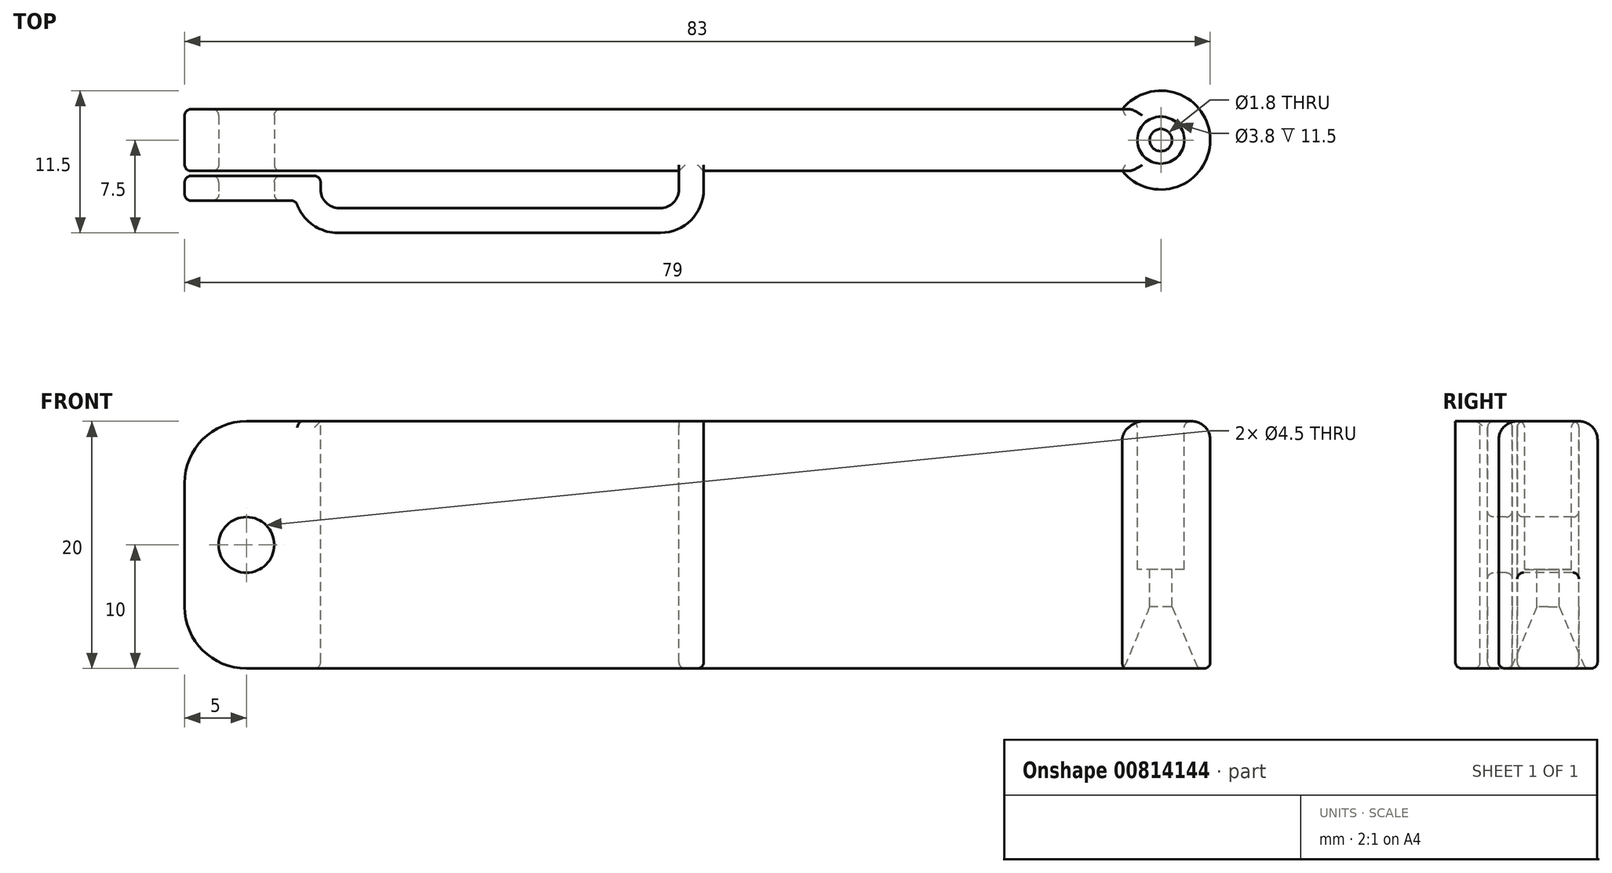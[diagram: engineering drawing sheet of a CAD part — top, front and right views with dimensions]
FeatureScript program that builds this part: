
annotation { "Feature Type Name" : "Feature", "Feature Type Description" : "" }
export const myFeature = defineFeature(function(context is Context, id is Id, definition is map)
    precondition{}
    {
        {
            var Q0;
            Q0=qCreatedBy(makeId("Front.planeOp"),FACE);
            var sketch = newSketch(context, id + "F0", { "sketchPlane" : qUnion([Q0])});
            skLineSegment(sketch, "E0.bottom", {"start": v(5, -20) * mm, "end": v(75, -20) * mm});
            skLineSegment(sketch, "E0.top", {"start": v(5, 0) * mm, "end": v(75, 0) * mm});
            skLineSegment(sketch, "E0.left", {"start": v(0, -15) * mm, "end": v(0, -5) * mm});
            skLineSegment(sketch, "E0.right", {"start": v(75, -20) * mm, "end": v(75, 0) * mm});
            skCircle(sketch, "E1", {"center": v(5, -10) * mm, "radius": 2.25 * mm});
            skPoint(sketch, "E2", {"position": v(0, -10) * mm});
            skPoint(sketch, "E3.visualSharp", {"position": v(0, 0) * mm});
            skArc(sketch, "E3.filletArc", {"start": v(5, 0) * mm, "mid": v(1.46, -1.46) * mm, "end": v(0, -5) * mm});
            skPoint(sketch, "E4.visualSharp", {"position": v(0, -20) * mm});
            skArc(sketch, "E4.filletArc", {"start": v(0, -15) * mm, "mid": v(1.46, -18.54) * mm, "end": v(5, -20) * mm});
            skSolve(sketch);
        }
        {
            var Q0;
            Q0 = qSketchRegion(id + "F0", true);
            extrude(context, id + "F1", {"entities" : qUnion([Q0]), "oppositeDirection" : true, "depth" : 5 * mm, "offsetDistance" : 25 * mm});
        }
        {
            var Q0;
            Q0=makeQuery(id+"F1.opExtrude","SWEPT_FACE",FACE,{"disambiguationData":[OSD([sQuery(id+"F0.wireOp",EDGE,"E0.top")])]});
            var sketch = newSketch(context, id + "F2", { "sketchPlane" : qUnion([Q0])});
            skLineSegment(sketch, "E5", {"start": v(0, 0) * mm, "end": v(11, 0) * mm});
            skLineSegment(sketch, "E6", {"start": v(11, 0) * mm, "end": v(11, -3) * mm});
            skLineSegment(sketch, "E7", {"start": v(11, -3) * mm, "end": v(40, -3) * mm});
            skLineSegment(sketch, "E8", {"start": v(40, -3) * mm, "end": v(40, 0) * mm});
            skLineSegment(sketch, "E9", {"start": v(40, 0) * mm, "end": v(42, 0) * mm});
            skLineSegment(sketch, "E10", {"start": v(42, 0) * mm, "end": v(42, -5) * mm});
            skLineSegment(sketch, "E11", {"start": v(42, -5) * mm, "end": v(9, -5) * mm});
            skLineSegment(sketch, "E12", {"start": v(9, -5) * mm, "end": v(9, -2.4) * mm});
            skLineSegment(sketch, "E13", {"start": v(0, -2.4) * mm, "end": v(0, 0) * mm});
            skLineSegment(sketch, "E14", {"start": v(0, -2.4) * mm, "end": v(9, -2.4) * mm});
            skSolve(sketch);
        }
        {
            var Q0;
            Q0 = qSketchRegion(id + "F2", true);
            var Q1;
            Q1=makeQuery(id+"F1.opExtrude","SWEPT_FACE",FACE,{"disambiguationData":[OSD([sQuery(id+"F0.wireOp",EDGE,"E0.bottom")])]});
            extrude(context, id + "F3", {"entities" : qUnion([Q0]), "operationType" : NewBodyOperationType.ADD, "endBound" : BoundingType.UP_TO_SURFACE, "oppositeDirection" : true, "depth" : 25 * mm, "endBoundEntityFace" : qUnion([Q1]), "offsetDistance" : 25 * mm});
        }
        {
            var Q0;
            Q0=makeQuery(id+"F1.opExtrude","CAP_FACE",FACE,{"disambiguationData":[OSD([sQuery(id+"F0.wireOp",EDGE,"E0.bottom"),sQuery(id+"F0.wireOp",EDGE,"E0.top"),sQuery(id+"F0.wireOp",EDGE,"E0.left"),sQuery(id+"F0.wireOp",EDGE,"E0.right"),sQuery(id+"F0.wireOp",EDGE,"E1"),sQuery(id+"F0.wireOp",EDGE,"E3.filletArc"),sQuery(id+"F0.wireOp",EDGE,"E4.filletArc")])],"isStart":false});
            var sketch = newSketch(context, id + "F4", { "sketchPlane" : qUnion([Q0])});
            skCircle(sketch, "E15", {"center": v(-5, -10) * mm, "radius": 2.25 * mm});
            skSolve(sketch);
        }
        {
            var Q0;
            Q0 = qSketchRegion(id + "F4", true);
            extrude(context, id + "F5", {"entities" : qUnion([Q0]), "operationType" : NewBodyOperationType.REMOVE, "endBound" : BoundingType.THROUGH_ALL, "oppositeDirection" : true, "depth" : 25 * mm, "offsetDistance" : 25 * mm});
        }
        {
            var Q0;
            Q0=makeQuery(id+"F3.opExtrude","CAP_EDGE",EDGE,{"disambiguationData":[OSD([sQuery(id+"F2.wireOp",EDGE,"E13")])],"isStart":false});
            var Q1;
            Q1=makeQuery(id+"F3.opExtrude","CAP_EDGE",EDGE,{"disambiguationData":[OSD([sQuery(id+"F2.wireOp",EDGE,"E13")])],"isStart":true});
            fillet(context, id + "F6", {"entities" : qUnion([Q0, Q1]), "radius" : 5 * mm, "tangentPropagation" : true, "allowEdgeOverflow" : false});
        }
        {
            var Q0;
            Q0=makeQuery(id+"F3.boolean.opBoolean","MERGE",FACE,{"derivedFrom":[makeQuery(id+"F1.opExtrude","SWEPT_FACE",FACE,{"disambiguationData":[OSD([sQuery(id+"F0.wireOp",EDGE,"E0.bottom")])]}),makeQuery(id+"F3.opExtrude","CAP_FACE",FACE,{"disambiguationData":[OSD([sQuery(id+"F2.wireOp",EDGE,"E5"),sQuery(id+"F2.wireOp",EDGE,"E6"),sQuery(id+"F2.wireOp",EDGE,"E7"),sQuery(id+"F2.wireOp",EDGE,"E8"),sQuery(id+"F2.wireOp",EDGE,"E9"),sQuery(id+"F2.wireOp",EDGE,"E10"),sQuery(id+"F2.wireOp",EDGE,"E11"),sQuery(id+"F2.wireOp",EDGE,"E12"),sQuery(id+"F2.wireOp",EDGE,"oNY84z7X-RgDA-BSrN-n4GT-R6lyssik0dSa"),sQuery(id+"F2.wireOp",EDGE,"E13")])],"isStart":false})]});
            var sketch = newSketch(context, id + "F7", { "sketchPlane" : qUnion([Q0])});
            skLineSegment(sketch, "E16.bottom", {"start": v(12.2, 0) * mm, "end": v(-0.8, 0) * mm});
            skLineSegment(sketch, "E16.top", {"start": v(12.2, 0.4) * mm, "end": v(-0.8, 0.4) * mm});
            skLineSegment(sketch, "E16.left", {"start": v(12.2, 0) * mm, "end": v(12.2, 0.4) * mm});
            skLineSegment(sketch, "E16.right", {"start": v(-0.8, 0) * mm, "end": v(-0.8, 0.4) * mm});
            skSolve(sketch);
        }
        {
            var Q0;
            Q0 = qSketchRegion(id + "F7", true);
            extrude(context, id + "F8", {"entities" : qUnion([Q0]), "operationType" : NewBodyOperationType.REMOVE, "endBound" : BoundingType.THROUGH_ALL, "oppositeDirection" : true, "depth" : 25 * mm, "offsetDistance" : 25 * mm});
        }
        {
            var Q0;
            Q0=makeQuery(id+"F1.opExtrude","SWEPT_EDGE",EDGE,{"disambiguationData":[OSD([sQuery(id+"F0.wireOp",EDGE,"E0.top"),sQuery(id+"F0.wireOp",EDGE,"E0.right")])]});
            cPoint(context, id + "F9", {"entities" : qUnion([Q0]), "parameter" : 0.5});
        }
        {
            var Q0;
            Q0=makeQuery(id+"F1.opExtrude","CAP_FACE",FACE,{"disambiguationData":[OSD([sQuery(id+"F0.wireOp",EDGE,"E0.bottom"),sQuery(id+"F0.wireOp",EDGE,"E0.top"),sQuery(id+"F0.wireOp",EDGE,"E0.left"),sQuery(id+"F0.wireOp",EDGE,"E0.right"),sQuery(id+"F0.wireOp",EDGE,"E1"),sQuery(id+"F0.wireOp",EDGE,"E3.filletArc"),sQuery(id+"F0.wireOp",EDGE,"E4.filletArc")])],"isStart":false});
            var Q1;
            Q1 = qCreatedBy(id + "F9" ,VERTEX);
            cPlane(context, id + "F10", {"entities" : qUnion([Q0, Q1]), "cplaneType" : CPlaneType.PLANE_POINT, "offset" : 25 * mm, "oppositeDirection" : true, "width" : 150 * mm, "height" : 150 * mm});
        }
        {
            var Q0;
            Q0=qCreatedBy(id+"F10.planeOp",FACE);
            var sketch = newSketch(context, id + "F11", { "sketchPlane" : qUnion([Q0])});
            skLineSegment(sketch, "E17", {"start": v(-78.1, -12) * mm, "end": v(-78.1, -15) * mm});
            skLineSegment(sketch, "E18", {"start": v(-78.1, -15) * mm, "end": v(-76, -20) * mm});
            skLineSegment(sketch, "E19", {"start": v(-76, -20) * mm, "end": v(-75, -20) * mm});
            skLineSegment(sketch, "E20", {"start": v(-75, -20) * mm, "end": v(-75, 0) * mm});
            skLineSegment(sketch, "E21", {"start": v(-75, 0) * mm, "end": v(-77.1, 0) * mm});
            skLineSegment(sketch, "E22", {"start": v(-79, 5.76) * mm, "end": v(-79, -23.82) * mm, "construction": true});
            skLineSegment(sketch, "E23", {"start": v(-77.1, 0) * mm, "end": v(-77.1, -12) * mm});
            skLineSegment(sketch, "E24", {"start": v(-77.1, -12) * mm, "end": v(-78.1, -12) * mm});
            skSolve(sketch);
        }
        {
            var Q0;
            Q0 = qSketchRegion(id + "F11", true);
            var Q1;
            Q1=sQuery(id+"F11.wireOp",EDGE,"E22");
            revolve(context, id + "F12", {"operationType" : NewBodyOperationType.ADD, "surfaceOperationType" : NewSurfaceOperationType.NEW, "entities" : qUnion([Q0]), "axis" : qUnion([Q1]), "revolveType" : RevolveType.FULL});
        }
        {
            var Q0;
            Q0=makeQuery(id+"F1.opExtrude","SWEPT_FACE",FACE,{"disambiguationData":[OSD([sQuery(id+"F0.wireOp",EDGE,"E0.right")])]});
            var sketch = newSketch(context, id + "F13", { "sketchPlane" : qUnion([Q0])});
            skLineSegment(sketch, "E25.bottom", {"start": v(5, 0) * mm, "end": v(0, 0) * mm});
            skLineSegment(sketch, "E25.top", {"start": v(5, -20) * mm, "end": v(0, -20) * mm});
            skLineSegment(sketch, "E25.left", {"start": v(5, 0) * mm, "end": v(5, -20) * mm});
            skLineSegment(sketch, "E25.right", {"start": v(0, 0) * mm, "end": v(0, -20) * mm});
            skSolve(sketch);
        }
        {
            var Q0;
            Q0 = qSketchRegion(id + "F13", true);
            var Q1;
            Q1=makeQuery(id+"F12.opRevolve","SWEPT_BODY",BODY,{"disambiguationData":[OSD([sQuery(id+"F11.wireOp",EDGE,"E17"),sQuery(id+"F11.wireOp",EDGE,"E18"),sQuery(id+"F11.wireOp",EDGE,"E19"),sQuery(id+"F11.wireOp",EDGE,"E20"),sQuery(id+"F11.wireOp",EDGE,"E21")])]});
            extrude(context, id + "F14", {"entities" : qUnion([Q0]), "operationType" : NewBodyOperationType.ADD, "depth" : 1 * mm, "endBoundEntityBody" : qUnion([Q1]), "offsetDistance" : 25 * mm});
        }
        {
            var Q0;
            Q0=makeQuery(id+"F3.opExtrude","SWEPT_EDGE",EDGE,{"disambiguationData":[OSD([sQuery(id+"F2.wireOp",EDGE,"E10"),sQuery(id+"F2.wireOp",EDGE,"E11")])]});
            var Q1;
            Q1=makeQuery(id+"F3.opExtrude","SWEPT_EDGE",EDGE,{"disambiguationData":[OSD([sQuery(id+"F2.wireOp",EDGE,"E11"),sQuery(id+"F2.wireOp",EDGE,"E12")])]});
            fillet(context, id + "F15", {"entities" : qUnion([Q0, Q1]), "radius" : 3.5 * mm, "tangentPropagation" : true, "allowEdgeOverflow" : false});
        }
        {
            var Q0;
            Q0=makeQuery(id+"F3.opExtrude","SWEPT_EDGE",EDGE,{"disambiguationData":[OSD([sQuery(id+"F2.wireOp",EDGE,"E7"),sQuery(id+"F2.wireOp",EDGE,"E8")])]});
            var Q1;
            Q1=makeQuery(id+"F3.opExtrude","SWEPT_EDGE",EDGE,{"disambiguationData":[OSD([sQuery(id+"F0.wireOp",EDGE,"E0.top"),sQuery(id+"F2.wireOp",EDGE,"E8"),sQuery(id+"F2.wireOp",EDGE,"E9")])]});
            var Q2;
            Q2=makeQuery(id+"F3.opExtrude","SWEPT_EDGE",EDGE,{"disambiguationData":[OSD([sQuery(id+"F2.wireOp",EDGE,"E6"),sQuery(id+"F2.wireOp",EDGE,"E7")])]});
            var Q3;
            Q3=makeQuery(id+"F3.opExtrude","SWEPT_EDGE",EDGE,{"disambiguationData":[OSD([sQuery(id+"F0.wireOp",EDGE,"E0.top"),sQuery(id+"F2.wireOp",EDGE,"E9"),sQuery(id+"F2.wireOp",EDGE,"E10")])]});
            fillet(context, id + "F16", {"entities" : qUnion([Q0, Q1, Q2, Q3]), "radius" : 1.5 * mm, "tangentPropagation" : true, "allowEdgeOverflow" : false});
        }
        {
            var Q0;
            Q0=makeQuery(id+"F12.opRevolve","SWEPT_EDGE",EDGE,{"disambiguationData":[OSD([sQuery(id+"F11.wireOp",EDGE,"E20"),sQuery(id+"F11.wireOp",EDGE,"E21")])]});
            fillet(context, id + "F17", {"entities" : qUnion([Q0]), "radius" : 1.5 * mm, "tangentPropagation" : true, "defaultsChanged" : true, "vertexSettings" : [], "allowEdgeOverflow" : false});
        }
        {
            var Q0;
            Q0=makeQuery(id+"F14.boolean.opBoolean","MERGE",FACE,{"derivedFrom":[makeQuery(id+"F3.boolean.opBoolean","MERGE",FACE,{"derivedFrom":[makeQuery(id+"F1.opExtrude","SWEPT_FACE",FACE,{"disambiguationData":[OSD([sQuery(id+"F0.wireOp",EDGE,"E0.bottom")])]}),makeQuery(id+"F3.opExtrude","CAP_FACE",FACE,{"disambiguationData":[OSD([sQuery(id+"F2.wireOp",EDGE,"E5"),sQuery(id+"F2.wireOp",EDGE,"E6"),sQuery(id+"F2.wireOp",EDGE,"E7"),sQuery(id+"F2.wireOp",EDGE,"E8"),sQuery(id+"F2.wireOp",EDGE,"E9"),sQuery(id+"F2.wireOp",EDGE,"E10"),sQuery(id+"F2.wireOp",EDGE,"E11"),sQuery(id+"F2.wireOp",EDGE,"E12"),sQuery(id+"F2.wireOp",EDGE,"E13"),sQuery(id+"F2.wireOp",EDGE,"E14")])],"isStart":false})]}),makeQuery(id+"F12.opRevolve","SWEPT_FACE",FACE,{"disambiguationData":[OSD([sQuery(id+"F11.wireOp",EDGE,"E19")])]}),makeQuery(id+"F14.opExtrude","SWEPT_FACE",FACE,{"disambiguationData":[OSD([sQuery(id+"F13.wireOp",EDGE,"E25.top")])]})]});
            var Q1;
            Q1=makeQuery(id+"F15.opFillet","BLEND_EDGE",EDGE,{"blendedFrom":[makeQuery(id+"F3.opExtrude","SWEPT_EDGE",EDGE,{"disambiguationData":[OSD([sQuery(id+"F2.wireOp",EDGE,"E11"),sQuery(id+"F2.wireOp",EDGE,"E12")])]}),makeQuery(id+"F3.opExtrude","SWEPT_FACE",FACE,{"disambiguationData":[OSD([sQuery(id+"F2.wireOp",EDGE,"E14")])]})],"blendedInto":[makeQuery(id+"F3.opExtrude","SWEPT_FACE",FACE,{"disambiguationData":[OSD([sQuery(id+"F2.wireOp",EDGE,"E14")])]})]});
            var Q2;
            Q2=makeQuery(id+"F12.opRevolve","SWEPT_EDGE",EDGE,{"disambiguationData":[OSD([sQuery(id+"F11.wireOp",EDGE,"E21"),sQuery(id+"F11.wireOp",EDGE,"E23")])]});
            var Q3;
            {var subQ2=sQuery(id+"F0.wireOp",EDGE,"E1");Q3=makeQuery(id+"F8.boolean.opBoolean","SPLIT",FACE,{"disambiguationData":[TD([makeQuery(id+"F8.opExtrude","SWEPT_FACE",FACE,{"disambiguationData":[OSD([sQuery(id+"F7.wireOp",EDGE,"E16.bottom")])]})])],"derivedFrom":makeQuery(id+"F5.boolean.opBoolean","MERGE",FACE,{"derivedFrom":[makeQuery(id+"F1.opExtrude","SWEPT_FACE",FACE,{"disambiguationData":[OSD([subQ2])]})],"fromTools":[makeQuery(id+"F5.opExtrude","SWEPT_FACE",FACE,{"disambiguationData":[OSD([sQuery(id+"F4.wireOp",EDGE,"E15")])]})]})});}
            var Q4;
            Q4=makeQuery(id+"F8.boolean.opBoolean","SPLIT",FACE,{"disambiguationData":[TD([makeQuery(id+"F3.opExtrude","SWEPT_FACE",FACE,{"disambiguationData":[OSD([sQuery(id+"F2.wireOp",EDGE,"E14")])]})])],"derivedFrom":makeQuery(id+"F5.boolean.opBoolean","MERGE",FACE,{"derivedFrom":[makeQuery(id+"F1.opExtrude","SWEPT_FACE",FACE,{"disambiguationData":[OSD([sQuery(id+"F0.wireOp",EDGE,"E1")])]})],"fromTools":[makeQuery(id+"F5.opExtrude","SWEPT_FACE",FACE,{"disambiguationData":[OSD([sQuery(id+"F4.wireOp",EDGE,"E15")])]})]})});
            var Q5;
            Q5=makeQuery(id+"F8.boolean.opBoolean","INTERSECT",EDGE,{"derivedFrom":[makeQuery(id+"F3.opExtrude","SWEPT_FACE",FACE,{"disambiguationData":[OSD([sQuery(id+"F2.wireOp",EDGE,"E6")])]}),makeQuery(id+"F8.opExtrude","SWEPT_FACE",FACE,{"disambiguationData":[OSD([sQuery(id+"F7.wireOp",EDGE,"E16.top")])]})]});
            fillet(context, id + "F18", {"entities" : qUnion([Q0, Q1, Q2, Q3, Q4, Q5]), "radius" : .5 * mm, "tangentPropagation" : true, "defaultsChanged" : false, "vertexSettings" : [], "allowEdgeOverflow" : false});
        }
    });
